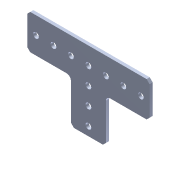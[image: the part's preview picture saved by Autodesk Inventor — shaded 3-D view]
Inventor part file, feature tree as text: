
AUTODESK INVENTOR PART (.ipt)
format: ipt  version: 2015 (Build 190159000, 159)  size: 131,072 bytes
history: native  units: in
note: dims shown in document units (in); Inventor stores cm internally (conversion verified against a paired STEP export)
features: fillet x1, other x1, imported_body x1
ambient origin geometry x8: Origin, YZ Plane, XZ Plane, XY Plane, X Axis, Y Axis, Z Axis, Center Point
bodies: Body1 (feature_tree)
feature tree (3):
  fillet  "Fillet1"  [1 undecoded]
  other  "217-3557-STEP1"
  imported_body  "Base1"
note: 1 required parameter value undecoded (feature->parameter linkage not recoverable at this tier; creation-order binding heuristic only, values carry confidence <= 0.55)
